# Revit family: Sanitary_Toilets_hansgrohe_60310XXX-GladeLake-S-Tank_bottom-water-supply
name_source: partatom
category: Plumbing Fixtures
units: mm (PartAtom-declared; Revit-internal decimal feet)

## family parameters
Cut with Voids When Loaded = No
Host = Face
Maintain Annotation Orientation = No
OmniClass Number = 23.31.19.00
OmniClass Title = Toilets
Part Type = Normal
Room Calculation Point = No
Round Connector Dimension = Use Diameter
Shared = No

## types (1)
- 450 White
    Connector Description = Water Inlet 12.7 mm
    Date Updated = 2025/01/13
    Default Elevation = 0 mm  [stored 0 ft]
    Description = GladeLake S Tank with bottom water supply
    Diameter = 13 mm  [stored 0.0426509 ft]
    Manufacturer = Hansgrohe
    Material 1 = Hansgrohe - Ceramic - 450 White
    Material 2 = Hansgrohe - Metal - Black
    Model = 60310XXX
    Product Page URL = https://www.hansgrohe.com
    Product data url = https://www.bimobject.com
    URL = https://www.hansgrohe.com
    Version = 1

note: [stored X ft] marks values corroborated as IEEE doubles in the binary element streams (Revit-internal decimal feet)

## geometry (parser evidence)
native form markers: Sweep x5
no freeform markers — native parametric forms only
